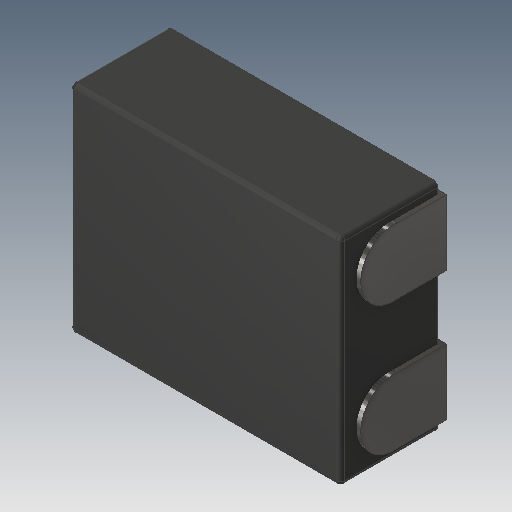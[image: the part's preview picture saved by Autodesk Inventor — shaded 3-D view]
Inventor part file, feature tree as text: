
AUTODESK INVENTOR PART (.ipt)
format: ipt  version: 2020 (Build 240168000, 168)  size: 156,672 bytes
history: native  units: mm
features: other x6, plane x3, extrude x2, sketch x2, mirror x1, fillet x1
ambient origin geometry x8: Origin, YZ Plane, XZ Plane, XY Plane, X Axis, Y Axis, Z Axis, Center Point
bodies: Body1 (feature_tree), Body2 (feature_tree), Body3 (feature_tree)
feature tree (15):
  other  "Sólido1"
  extrude  "Extrusión1"  Depth=1.0mm
  plane  "Plano de trabajo1"
  extrude  "Extrusión2"  TaperAngle=90.0deg  [1 undecoded]
  other  "Edición directa1"
  plane  "Plano de trabajo3"
  mirror  "Simetría1"
  fillet  "Empalme1"  Radius=0.3mm
  sketch  "Boceto1"  dims[d0=1.25mm d1=1.0mm]
  sketch  "Boceto2"  dims[d2=0.45mm d3=0.0mm d4=90.0deg d5=0.3mm d6=0.0mm d7=0.0mm d8=-0.02mm d9=-0.02mm d10=90.0deg d11=0.02mm]
  other  "Sólido2"
  plane  "Plano de trabajo2"
  other  "Patrón de Sólido2:1"
  other  "Sólido3"
  other  "Desplazar1"
note: 1 required parameter value undecoded (feature->parameter linkage not recoverable at this tier; creation-order binding heuristic only, values carry confidence <= 0.55)
